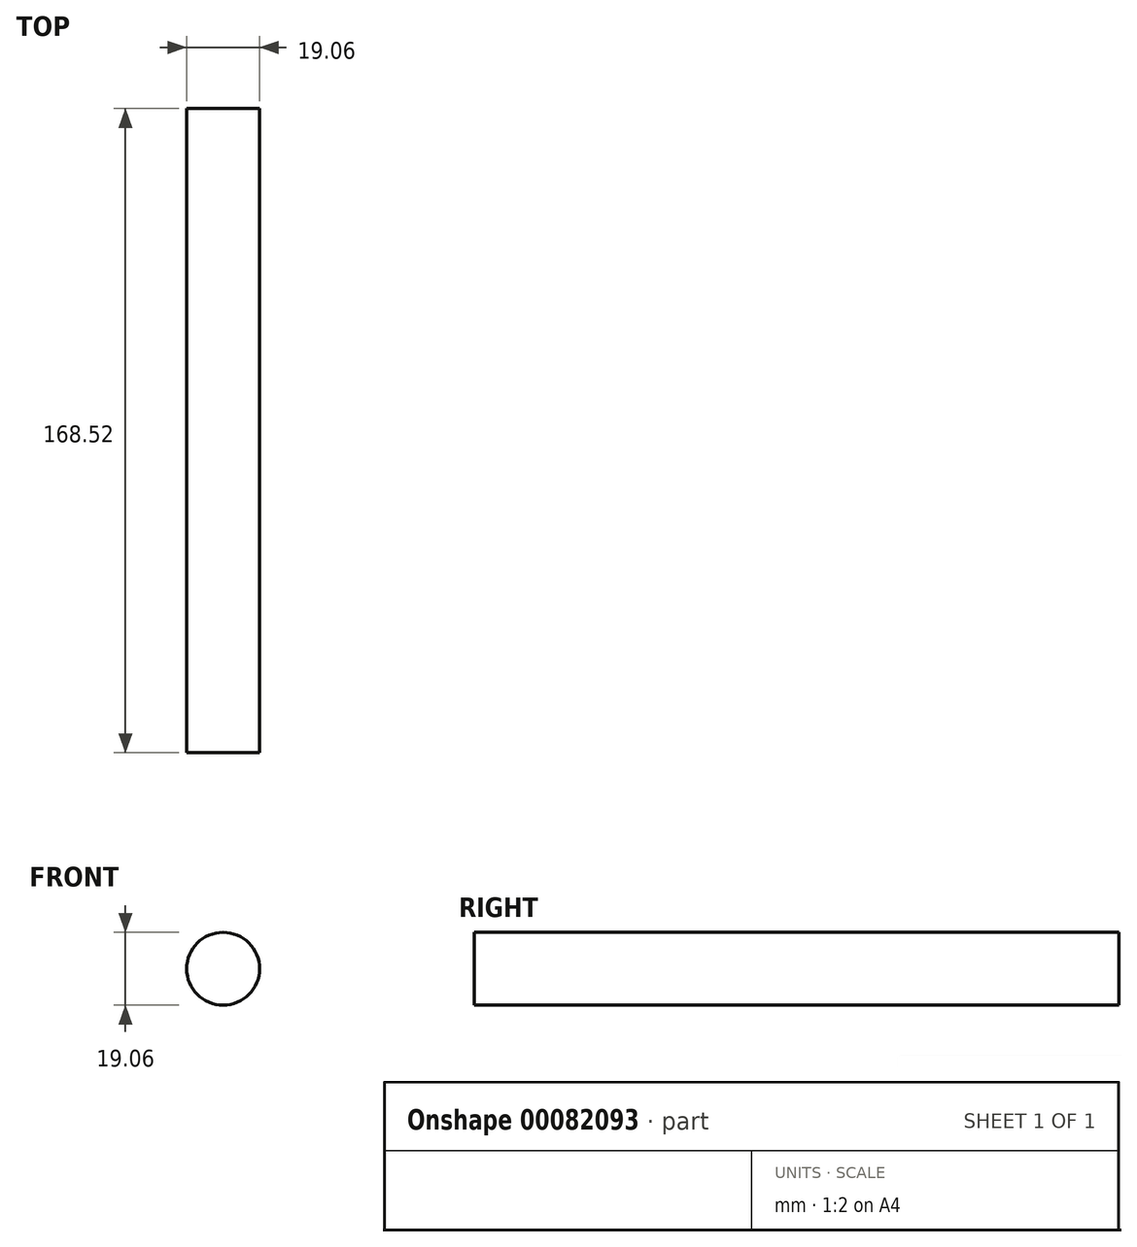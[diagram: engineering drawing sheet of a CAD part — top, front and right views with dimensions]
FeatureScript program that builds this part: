
annotation { "Feature Type Name" : "Feature", "Feature Type Description" : "" }
export const myFeature = defineFeature(function(context is Context, id is Id, definition is map)
    precondition{}
    {
        {
            var Q0;
            Q0=qCreatedBy(makeId("Front.planeOp"),FACE);
            var sketch = newSketch(context, id + "F0", { "sketchPlane" : qUnion([Q0])});
            skCircle(sketch, "E0", {"center": v(0, 0) * mm, "radius": 9.53 * mm});
            skSolve(sketch);
        }
        {
            var Q0;
            Q0=makeQuery(id+"F0.imprint","IMPRINT",FACE,{"disambiguationData":[TD([[makeQuery(id+"F0.imprint","IMPRINT",EDGE,{"derivedFrom":sQuery(id+"F0.wireOp",EDGE,"E0")}),1.0]])]});
            extrude(context, id + "F1", {"entities" : qUnion([Q0]), "endBound" : BoundingType.SYMMETRIC, "depth" : 168.53 * mm});
        }
    });
